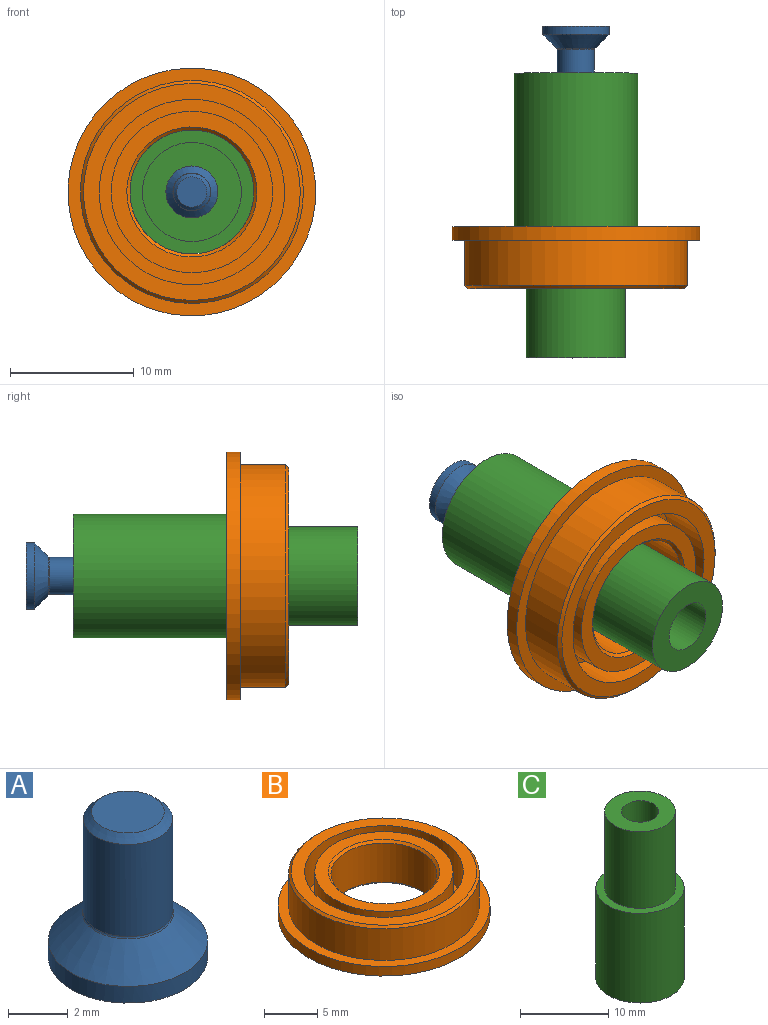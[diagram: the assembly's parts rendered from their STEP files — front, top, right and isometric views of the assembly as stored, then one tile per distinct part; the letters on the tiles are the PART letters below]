
ASSEMBLY  parts=3 mates=2
PART A: 20 faces, bbox 5.4x5.4x6 mm
  f0: cylinder r=2.67mm len=5.35mm, axis (0,0,-1), area 11.5mm2, adj f1,f15
  f1: plane 5.35x5.35mm, normal (0,0,-1), area 19mm2, adj f0,f2,f3,f4,f5,f6,f7
  f2: plane 1.1x1mm, normal (0.5,-0.87,0), area 1.3mm2, adj f1,f3,f7,f8,f9
  f3: plane 1.1x1mm, normal (-0.5,-0.87,0), area 1.3mm2, adj f1,f2,f4,f9,f10
  f4: plane 1.15x1.1mm, normal (-1,0,0), area 1.3mm2, adj f1,f3,f5,f10,f11
  f5: plane 1.1x1mm, normal (-0.5,0.87,0), area 1.3mm2, adj f1,f4,f6,f11,f12
  f6: plane 1.1x1mm, normal (0.5,0.87,0), area 1.3mm2, adj f1,f5,f7,f12,f13
  f7: plane 1.15x1.1mm, normal (1,0,0), area 1.3mm2, adj f1,f2,f6,f8,f13
  f8: plane 0.87x0.5mm, normal (0,0,-1), area 0.1mm2, adj f2,f7,f14
  f9: plane 1x0.29mm, normal (0,0,-1), area 0.1mm2, adj f2,f3,f14
  f10: plane 0.87x0.5mm, normal (0,0,-1), area 0.1mm2, adj f3,f4,f14
  f11: plane 0.87x0.5mm, normal (0,0,-1), area 0.1mm2, adj f4,f5,f14
  f12: plane 1x0.29mm, normal (0,0,-1), area 0.1mm2, adj f5,f6,f14
  f13: plane 0.87x0.5mm, normal (0,0,-1), area 0.1mm2, adj f6,f7,f14
  f14: cone r=0mm half-angle=59deg, axis (0,0,-1), area 3.7mm2, adj f8,f9,f10,f11,f12,f13
  f15: cone r=1.5mm half-angle=45deg, axis (0,0,-1), area 21.4mm2, adj f0,f18
  f16: plane 2.44x2.44mm, normal (0,0,1), area 4.7mm2, adj f19
  f17: cylinder r=1.5mm len=3.79mm, axis (0,0,-1), area 35.7mm2, adj f18,f19
  f18: torus R=1.6mm, axis (0,0,-1), area 0.7mm2, adj f15,f17
  f19: cone r=1.22mm half-angle=45deg, axis (0,0,-1), area 3.4mm2, adj f16,f17
PART B: 17 faces, bbox 20x20x5 mm
  f0: cone r=5.25mm half-angle=45deg, axis (0,0,-1), area 11.4mm2, adj f1,f16
  f1: plane 13.03x13.03mm, normal (0,0,-1), area 46.8mm2, adj f0,f2
  f2: cylinder r=6.52mm len=13.03mm, axis (0,0,-1), area 17.5mm2, adj f1,f3
  f3: plane 14.97x14.97mm, normal (0,0,-1), area 42.5mm2, adj f2,f4
  f4: cylinder r=7.48mm len=14.97mm, axis (0,0,-1), area 20.1mm2, adj f3,f5
  f5: plane 20x20mm, normal (0,0,-1), area 138.2mm2, adj f4,f6
  f6: cylinder r=10mm len=20mm, axis (0,0,-1), area 69.1mm2, adj f5,f7
  f7: plane 20x20mm, normal (0,0,1), area 59.7mm2, adj f6,f8
  f8: cylinder r=9mm len=18mm, axis (0,0,-1), area 206.4mm2, adj f7,f9
  f9: cone r=9mm half-angle=45deg, axis (0,0,-1), area 19.7mm2, adj f8,f10
  f10: plane 17.5x17.5mm, normal (0,0,1), area 64.6mm2, adj f9,f11
  f11: cylinder r=7.48mm len=14.97mm, axis (0,0,-1), area 183.4mm2, adj f10,f12
  f12: plane 14.97x14.97mm, normal (0,0,1), area 42.5mm2, adj f11,f13
  f13: cylinder r=6.52mm len=13.04mm, axis (0,0,-1), area 159.7mm2, adj f12,f14
  f14: plane 13.04x13.04mm, normal (0,0,1), area 46.8mm2, adj f13,f15
  f15: cone r=5mm half-angle=45deg, axis (0,0,1), area 11.4mm2, adj f14,f16
  f16: cylinder r=5mm len=10mm, axis (0,0,-1), area 141.4mm2, adj f0,f15
PART C: 6 faces, bbox 10x10x23 mm
  f0: cylinder r=5mm len=12.4mm, axis (0,0,-1), area 389.6mm2, adj f1,f2
  f1: plane 10x10mm, normal (0,0,1), area 28.3mm2, adj f0,f3
  f2: plane 10x10mm, normal (0,0,-1), area 64.7mm2, adj f0,f4
  f3: cylinder r=4mm len=10.6mm, axis (0,0,-1), area 266.4mm2, adj f1,f5
  f4: cylinder r=2.1mm len=23mm, axis (0,0,-1), area 303.5mm2, adj f2,f5
  f5: plane 8x8mm, normal (0,0,1), area 36.4mm2, adj f3,f4
PLACE A rot(axis=(0.73,0.49,-0.49),108deg) t=(-45.72,-0.66,41.77)mm
PLACE B rot(axis=(0.5,0.61,-0.61),127.2deg) t=(-67.35,-0.96,61.95)mm
PLACE C rot(axis=(0.34,-0.66,0.66),142.1deg) t=(-13.04,-0.96,135.14)mm
MATE revolute C.f0 <-> B.f0  axis (0,-1,0) through (-24.12,10.14,86.62)mm
MATE revolute A.f0 <-> C.f0  axis (0,1,0) through (-24.12,22.54,86.62)mm
